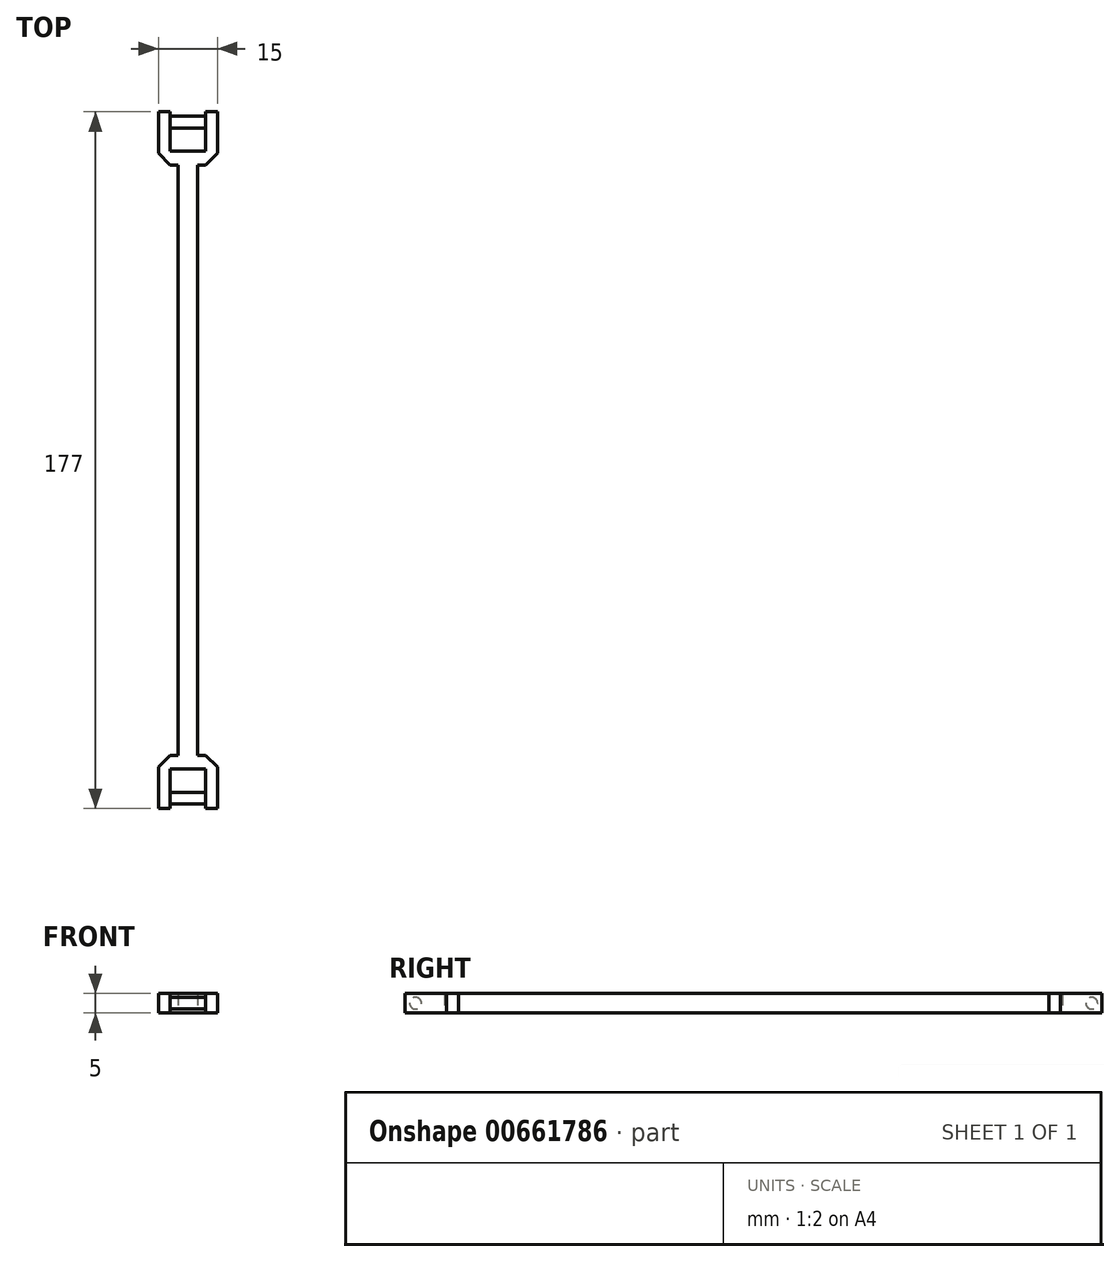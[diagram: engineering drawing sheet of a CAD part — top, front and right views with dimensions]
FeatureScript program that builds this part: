
annotation { "Feature Type Name" : "Feature", "Feature Type Description" : "" }
export const myFeature = defineFeature(function(context is Context, id is Id, definition is map)
    precondition{}
    {
        {
            var Q0;
            Q0=qCreatedBy(makeId("Top.planeOp"),FACE);
            var sketch = newSketch(context, id + "F0", { "sketchPlane" : qUnion([Q0])});
            skLineSegment(sketch, "E0.bottom", {"start": v(2.5, 75) * mm, "end": v(-2.5, 75) * mm});
            skLineSegment(sketch, "E0.top", {"start": v(2.5, -75) * mm, "end": v(-2.5, -75) * mm});
            skLineSegment(sketch, "E0.left", {"start": v(2.5, 75) * mm, "end": v(2.5, -75) * mm});
            skLineSegment(sketch, "E0.right", {"start": v(-2.5, 75) * mm, "end": v(-2.5, -75) * mm});
            skPoint(sketch, "E0.middle", {"position": v(0, 0) * mm});
            skLineSegment(sketch, "E1", {"start": v(2.5, 75) * mm, "end": v(7.5, 75) * mm});
            skLineSegment(sketch, "E2", {"start": v(7.5, 75) * mm, "end": v(7.5, 88.5) * mm});
            skLineSegment(sketch, "E3", {"start": v(7.5, 88.5) * mm, "end": v(4.5, 88.5) * mm});
            skLineSegment(sketch, "E4", {"start": v(4.5, 88.5) * mm, "end": v(4.5, 78.5) * mm});
            skLineSegment(sketch, "E5", {"start": v(4.5, 78.5) * mm, "end": v(0, 78.5) * mm});
            skLineSegment(sketch, "E6.MirrorCS", {"start": v(-2.5, 75) * mm, "end": v(-7.5, 75) * mm});
            skLineSegment(sketch, "E7.MirrorCS", {"start": v(-7.5, 75) * mm, "end": v(-7.5, 88.5) * mm});
            skLineSegment(sketch, "E8.MirrorCS", {"start": v(-4.5, 88.5) * mm, "end": v(-4.5, 78.5) * mm});
            skLineSegment(sketch, "E9.MirrorCS", {"start": v(-4.5, 78.5) * mm, "end": v(0, 78.5) * mm});
            skLineSegment(sketch, "E10.MirrorCS", {"start": v(-7.5, 88.5) * mm, "end": v(-4.5, 88.5) * mm});
            skSolve(sketch);
        }
        {
            var Q0;
            Q0 = qSketchRegion(id + "F0", true);
            extrude(context, id + "F1", {"entities" : qUnion([Q0]), "depth" : 5 * mm, "offsetDistance" : 25 * mm});
        }
        {
            var Q0;
            Q0=makeQuery(id+"F1.opExtrude","SWEPT_FACE",FACE,{"disambiguationData":[OSD([sQuery(id+"F0.wireOp",EDGE,"E4")])]});
            var sketch = newSketch(context, id + "F2", { "sketchPlane" : qUnion([Q0])});
            skCircle(sketch, "E11", {"center": v(-85.9, 2.5) * mm, "radius": 1.5 * mm});
            skPoint(sketch, "E11.centerSnap0", {"position": v(-88.5, 2.5) * mm});
            skSolve(sketch);
        }
        {
            var Q0;
            Q0 = qSketchRegion(id + "F2", true);
            var Q1;
            Q1=makeQuery(id+"F1.opExtrude","SWEPT_FACE",FACE,{"disambiguationData":[OSD([sQuery(id+"F0.wireOp",EDGE,"E8.MirrorCS")])]});
            extrude(context, id + "F3", {"entities" : qUnion([Q0]), "operationType" : NewBodyOperationType.ADD, "endBound" : BoundingType.UP_TO_SURFACE, "depth" : 25 * mm, "endBoundEntityFace" : qUnion([Q1]), "offsetDistance" : 25 * mm});
        }
        {
            var Q0;
            Q0=makeQuery(id+"F1.opExtrude","SWEPT_BODY",BODY,{"disambiguationData":[OSD([sQuery(id+"F0.wireOp",EDGE,"E0.top"),sQuery(id+"F0.wireOp",EDGE,"E0.left"),sQuery(id+"F0.wireOp",EDGE,"E0.right"),sQuery(id+"F0.wireOp",EDGE,"E1"),sQuery(id+"F0.wireOp",EDGE,"E2"),sQuery(id+"F0.wireOp",EDGE,"E3"),sQuery(id+"F0.wireOp",EDGE,"E4"),sQuery(id+"F0.wireOp",EDGE,"E5"),sQuery(id+"F0.wireOp",EDGE,"E6.MirrorCS"),sQuery(id+"F0.wireOp",EDGE,"E7.MirrorCS"),sQuery(id+"F0.wireOp",EDGE,"E8.MirrorCS"),sQuery(id+"F0.wireOp",EDGE,"E9.MirrorCS"),sQuery(id+"F0.wireOp",EDGE,"E10.MirrorCS")])]});
            var Q1;
            Q1=qCreatedBy(makeId("Front.planeOp"),FACE);
            mirror(context, id + "F4", {"operationType" : NewBodyOperationType.ADD, "entities" : qUnion([Q0]), "mirrorPlane" : qUnion([Q1])});
        }
        {
            var Q0;
            Q0=makeQuery(id+"F1.opExtrude","SWEPT_EDGE",EDGE,{"disambiguationData":[OSD([sQuery(id+"F0.wireOp",EDGE,"E6.MirrorCS"),sQuery(id+"F0.wireOp",EDGE,"E7.MirrorCS")])]});
            var Q1;
            Q1=makeQuery(id+"F1.opExtrude","SWEPT_EDGE",EDGE,{"disambiguationData":[OSD([sQuery(id+"F0.wireOp",EDGE,"E1"),sQuery(id+"F0.wireOp",EDGE,"E2")])]});
            var Q2;
            Q2=makeQuery(id+"F4.opPattern","COPY",EDGE,{"derivedFrom":makeQuery(id+"F1.opExtrude","SWEPT_EDGE",EDGE,{"disambiguationData":[OSD([sQuery(id+"F0.wireOp",EDGE,"E6.MirrorCS"),sQuery(id+"F0.wireOp",EDGE,"E7.MirrorCS")])]}),"instanceName":"1"});
            var Q3;
            Q3=makeQuery(id+"F4.opPattern","COPY",EDGE,{"derivedFrom":makeQuery(id+"F1.opExtrude","SWEPT_EDGE",EDGE,{"disambiguationData":[OSD([sQuery(id+"F0.wireOp",EDGE,"E1"),sQuery(id+"F0.wireOp",EDGE,"E2")])]}),"instanceName":"1"});
            chamfer(context, id + "F5", {"entities" : qUnion([Q0, Q1, Q2, Q3]), "width" : 3 * mm, "tangentPropagation" : true});
        }
    });
